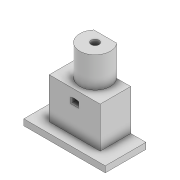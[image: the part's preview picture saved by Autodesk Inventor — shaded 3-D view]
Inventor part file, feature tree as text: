
AUTODESK INVENTOR PART (.ipt)
format: ipt  version: 2022 (Build 260153000, 153)  size: 177,152 bytes
history: native  units: mm
features: extrude x9, sketch x9, projected_geometry x2
ambient origin geometry x8: Origin, YZ Plane, XZ Plane, XY Plane, X Axis, Y Axis, Z Axis, Center Point
bodies: Solid1 (feature_tree)
feature tree (20):
  extrude  "Extrusion1"  Depth=25.0mm
  extrude  "Extrusion2"  Depth=20.0mm TaperAngle=0.0deg
  extrude  "Extrusion3"  Depth=100.0mm TaperAngle=0.0deg
  extrude  "Extrusion4"  Depth=15.0mm TaperAngle=0.0deg
  extrude  "Extrusion6"  Depth=40.0mm
  extrude  "Extrusion8"  Depth=10.0mm TaperAngle=0.0deg
  extrude  "Extrusion9"  Depth=2.0mm
  extrude  "Extrusion10"  Depth=3.0mm
  extrude  "Extrusion11"  Depth=15.0mm
  sketch  "Sketch1"  dims[d0=12.2mm d1=25.0mm]
  sketch  "Sketch2"  dims[d2=20.0mm d3=20.0mm d4=0.0mm]
  sketch  "Sketch3"  dims[d5=3.9mm d6=100.0mm d7=0.0mm]
  projected_geometry  "Projected Loop1"
  sketch  "Sketch4"  dims[d8=15.0mm d9=15.0mm d10=0.0mm]
  sketch  "Sketch6"  dims[d11=30.0mm d12=40.0mm]
  sketch  "Sketch8"  dims[d13=3.0mm d14=0.0mm d21=10.0mm d22=0.0mm]
  sketch  "Sketch9"  dims[d26=100.0mm d27=0.0mm d28=2.0mm]
  projected_geometry  "Projected Loop3"
  sketch  "Sketch10"  dims[d29=2.0mm d30=3.0mm]
  sketch  "Sketch11"  dims[d31=5.0mm d32=0.0mm d33=9.8mm d34=15.0mm d35=0.0mm d36=100.0mm d37=0.0mm]
